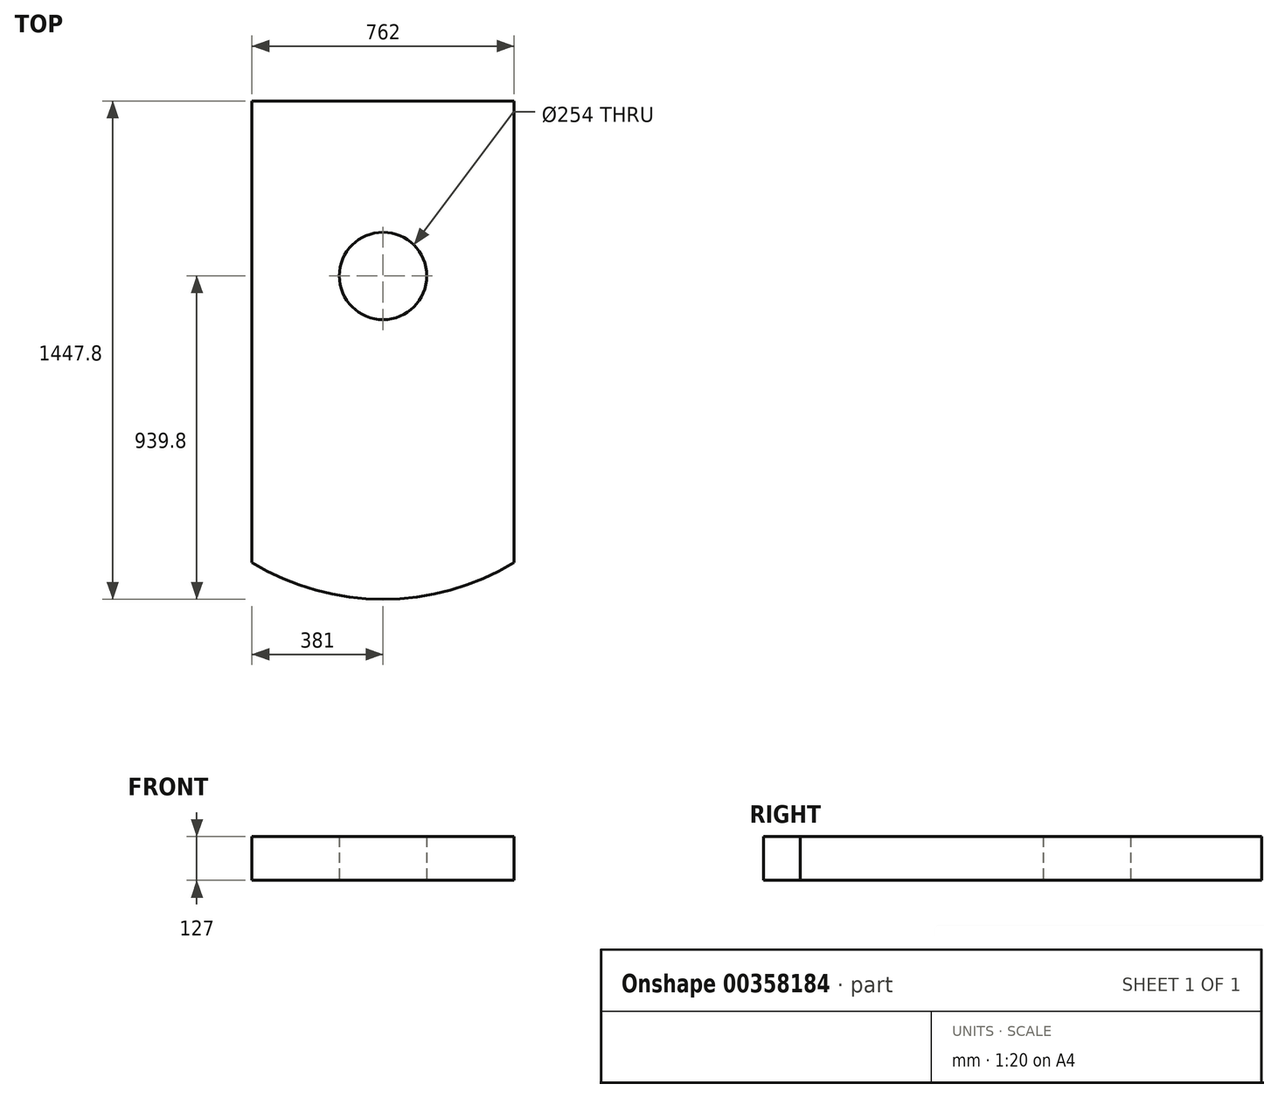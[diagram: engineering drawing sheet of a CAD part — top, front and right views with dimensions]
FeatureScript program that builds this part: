
annotation { "Feature Type Name" : "Feature", "Feature Type Description" : "" }
export const myFeature = defineFeature(function(context is Context, id is Id, definition is map)
    precondition{}
    {
        {
            var Q0;
            Q0=qCreatedBy(makeId("Top.planeOp"),FACE);
            var sketch = newSketch(context, id + "F0", { "sketchPlane" : qUnion([Q0])});
            skCircle(sketch, "E0", {"center": v(0, 0) * mm, "radius": 127 * mm});
            skLineSegment(sketch, "E1.top", {"start": v(381, 508) * mm, "end": v(-381, 508) * mm});
            skLineSegment(sketch, "E1.left", {"start": v(381, 0) * mm, "end": v(381, 508) * mm});
            skLineSegment(sketch, "E1.right", {"start": v(-381, 0) * mm, "end": v(-381, 508) * mm});
            skPoint(sketch, "E1.middle", {"position": v(0, 254) * mm});
            skArc(sketch, "E2", {"start": v(-381, -833.61) * mm, "mid": v(0, -939.8) * mm, "end": v(381, -833.61) * mm});
            skLineSegment(sketch, "E3", {"start": v(-381, 0) * mm, "end": v(-381, -833.61) * mm});
            skLineSegment(sketch, "E4", {"start": v(381, 0) * mm, "end": v(381, -833.61) * mm});
            skSolve(sketch);
        }
        {
            var Q0;
            Q0 = qSketchRegion(id + "F0", true);
            extrude(context, id + "F1", {"entities" : qUnion([Q0]), "depth" : 127 * mm});
        }
    });
